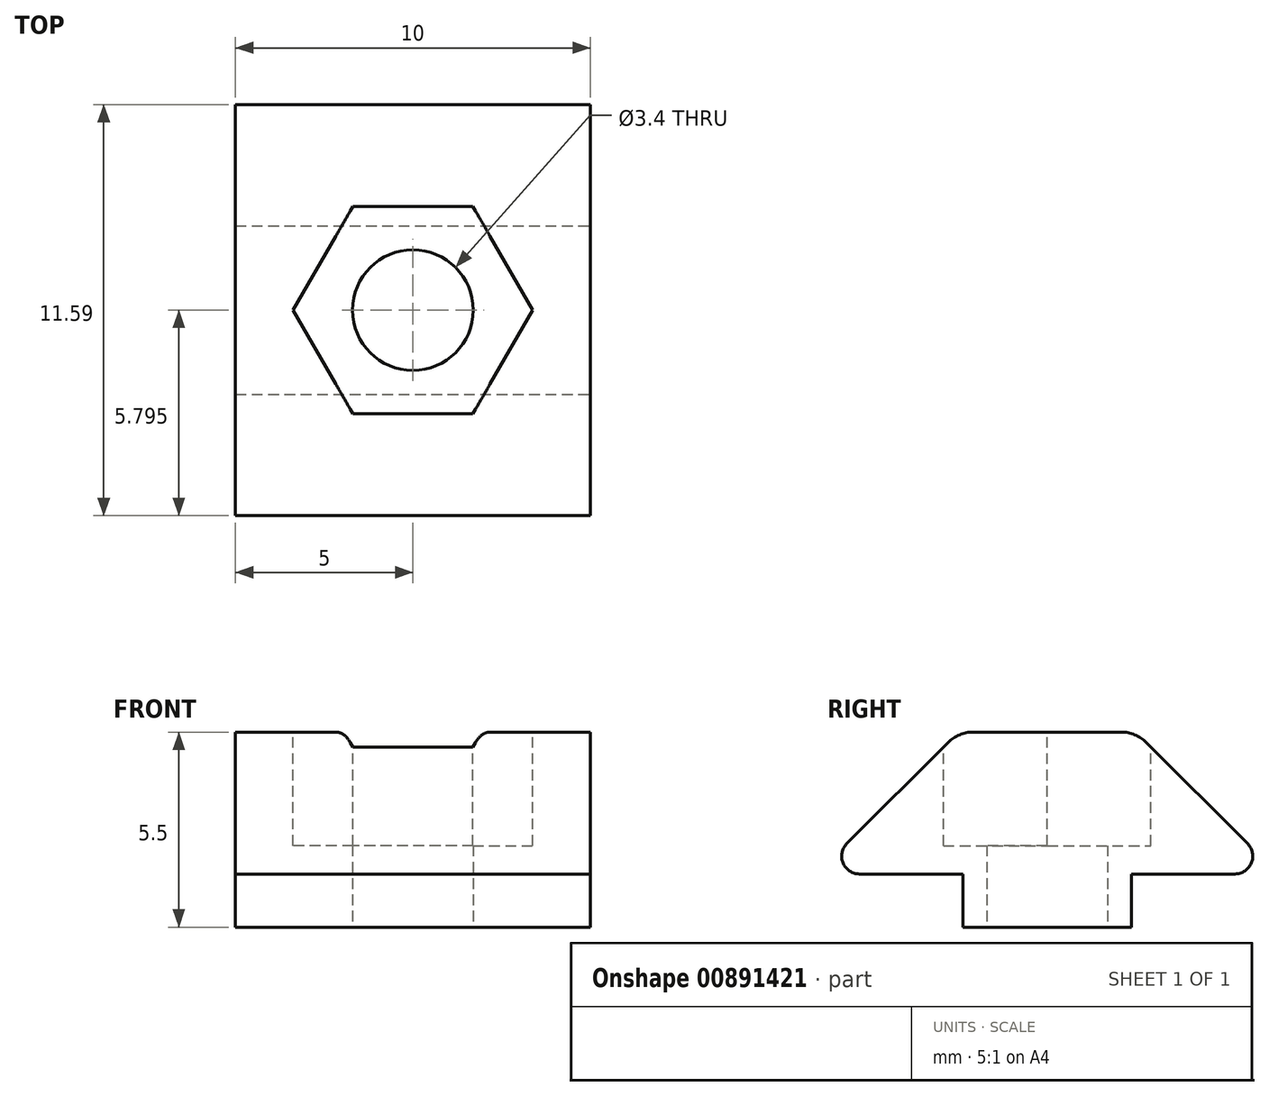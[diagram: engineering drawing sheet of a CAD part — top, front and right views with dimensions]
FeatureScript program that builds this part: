
annotation { "Feature Type Name" : "Feature", "Feature Type Description" : "" }
export const myFeature = defineFeature(function(context is Context, id is Id, definition is map)
    precondition{}
    {
        {
            var Q0;
            Q0=qCreatedBy(makeId("Top.planeOp"),FACE);
            var sketch = newSketch(context, id + "F0", { "sketchPlane" : qUnion([Q0])});
            skLineSegment(sketch, "E0.bottom", {"start": v(0, 4.75) * mm, "end": v(10, 4.75) * mm});
            skLineSegment(sketch, "E0.top", {"start": v(0, 0) * mm, "end": v(10, 0) * mm});
            skLineSegment(sketch, "E0.left", {"start": v(0, 4.75) * mm, "end": v(0, 0) * mm});
            skLineSegment(sketch, "E0.right", {"start": v(10, 4.75) * mm, "end": v(10, 0) * mm});
            skSolve(sketch);
        }
        {
            var Q0;
            Q0=makeQuery(id+"F0.imprint","IMPRINT",FACE,{"disambiguationData":[TD([[makeQuery(id+"F0.imprint","IMPRINT",EDGE,{"derivedFrom":sQuery(id+"F0.wireOp",EDGE,"E0.bottom")}),-1.0]])]});
            extrude(context, id + "F1", {"entities" : qUnion([Q0]), "depth" : 1.5 * mm, "offsetDistance" : 25 * mm});
        }
        {
            var Q0;
            Q0=makeQuery(id+"F1.opExtrude","CAP_FACE",FACE,{"disambiguationData":[OSD([sQuery(id+"F0.wireOp",EDGE,"E0.bottom"),sQuery(id+"F0.wireOp",EDGE,"E0.top"),sQuery(id+"F0.wireOp",EDGE,"E0.left"),sQuery(id+"F0.wireOp",EDGE,"E0.right")])],"isStart":false});
            var sketch = newSketch(context, id + "F2", { "sketchPlane" : qUnion([Q0])});
            skLineSegment(sketch, "E1.bottom", {"start": v(0, 8.88) * mm, "end": v(10, 8.88) * mm});
            skLineSegment(sketch, "E1.top", {"start": v(0, -4.13) * mm, "end": v(10, -4.13) * mm});
            skLineSegment(sketch, "E1.left", {"start": v(0, 8.87) * mm, "end": v(0, -4.13) * mm});
            skLineSegment(sketch, "E1.right", {"start": v(10, 8.88) * mm, "end": v(10, -4.13) * mm});
            skPoint(sketch, "E2", {"position": v(10, 2.37) * mm});
            skPoint(sketch, "E3", {"position": v(0, 2.37) * mm});
            skLineSegment(sketch, "E4", {"start": v(0, 2.37) * mm, "end": v(10, 2.37) * mm, "construction": true});
            skSolve(sketch);
        }
        {
            var Q0;
            {var subQ0=sQuery(id+"F2.wireOp",EDGE,"E1.top");Q0=makeQuery(id+"F2.imprint","IMPRINT",FACE,{"disambiguationData":[TD([[makeQuery(id+"F2.imprint","IMPRINT",EDGE,{"derivedFrom":subQ0}),1.0]])]});}
            var Q1;
            {var subQ1=makeQuery(id+"F1.opExtrude","CAP_EDGE",EDGE,{"disambiguationData":[OSD([sQuery(id+"F0.wireOp",EDGE,"E0.bottom")])],"isStart":false});Q1=makeQuery(id+"F2.imprint","IMPRINT",FACE,{"disambiguationData":[TD([[makeQuery(id+"F2.imprint","IMPRINT",EDGE,{"derivedFrom":subQ1}),-1.0]])]});}
            var Q2;
            {var subQ0=sQuery(id+"F2.wireOp",EDGE,"E1.bottom");Q2=makeQuery(id+"F2.imprint","IMPRINT",FACE,{"disambiguationData":[TD([[makeQuery(id+"F2.imprint","IMPRINT",EDGE,{"derivedFrom":subQ0}),-1.0]])]});}
            extrude(context, id + "F3", {"entities" : qUnion([Q0, Q1, Q2]), "operationType" : NewBodyOperationType.ADD, "depth" : 4 * mm, "offsetDistance" : 25 * mm});
        }
        {
            var Q0;
            Q0=makeQuery(id+"F3.opExtrude","CAP_EDGE",EDGE,{"disambiguationData":[OSD([sQuery(id+"F2.wireOp",EDGE,"E1.bottom")])],"isStart":false});
            var Q1;
            Q1=makeQuery(id+"F3.opExtrude","CAP_EDGE",EDGE,{"disambiguationData":[OSD([sQuery(id+"F2.wireOp",EDGE,"E1.top")])],"isStart":false});
            chamfer(context, id + "F4", {"entities" : qUnion([Q0, Q1]), "width" : 4 * mm, "tangentPropagation" : true});
        }
        {
            var Q0;
            Q0=makeQuery(id+"F3.opExtrude","CAP_FACE",FACE,{"disambiguationData":[OSD([sQuery(id+"F2.wireOp",EDGE,"E1.bottom"),sQuery(id+"F2.wireOp",EDGE,"E1.top"),sQuery(id+"F2.wireOp",EDGE,"E1.left"),sQuery(id+"F2.wireOp",EDGE,"E1.right")])],"isStart":false});
            var sketch = newSketch(context, id + "F5", { "sketchPlane" : qUnion([Q0])});
            skLineSegment(sketch, "E5", {"start": v(5, 4.88) * mm, "end": v(5, -0.13) * mm, "construction": true});
            skLineSegment(sketch, "E6", {"start": v(0, 2.38) * mm, "end": v(10, 2.38) * mm, "construction": true});
            skCircle(sketch, "E7.cCircle", {"center": v(5, 2.38) * mm, "radius": 2.93 * mm, "construction": true});
            skLineSegment(sketch, "E7.0", {"start": v(3.31, 5.3) * mm, "end": v(6.69, 5.3) * mm});
            skLineSegment(sketch, "E7.1", {"start": v(6.69, 5.3) * mm, "end": v(8.38, 2.38) * mm});
            skLineSegment(sketch, "E7.2", {"start": v(8.38, 2.38) * mm, "end": v(6.69, -0.55) * mm});
            skLineSegment(sketch, "E7.3", {"start": v(6.69, -0.55) * mm, "end": v(3.31, -0.55) * mm});
            skLineSegment(sketch, "E7.4", {"start": v(3.31, -0.55) * mm, "end": v(1.62, 2.38) * mm});
            skLineSegment(sketch, "E7.5", {"start": v(1.62, 2.38) * mm, "end": v(3.31, 5.3) * mm});
            skPoint(sketch, "E7.0.midPoint", {"position": v(5, 5.3) * mm});
            skSolve(sketch);
        }
        {
            var Q0;
            {var subQ0=sQuery(id+"F5.wireOp",EDGE,"E7.0");Q0=makeQuery(id+"F5.imprint","IMPRINT",FACE,{"disambiguationData":[TD([[makeQuery(id+"F5.imprint","IMPRINT",EDGE,{"derivedFrom":subQ0}),-1.0]])]});}
            var Q1;
            {var subQ8=sQuery(id+"F5.wireOp",EDGE,"E7.2");var subQ9=sQuery(id+"F5.wireOp",EDGE,"E7.1");var subQ10=makeQuery(id+"F5.imprint","INTERSECT",VERTEX,{"derivedFrom":[subQ9,subQ8]});Q1=makeQuery(id+"F5.imprint","IMPRINT",FACE,{"disambiguationData":[TD([[makeQuery(id+"F5.imprint","IMPRINT",EDGE,{"disambiguationData":[TD([[subQ10,1.0]])],"derivedFrom":subQ9}),-1.0]])]});}
            var Q2;
            {var subQ0=sQuery(id+"F5.wireOp",EDGE,"E7.3");Q2=makeQuery(id+"F5.imprint","IMPRINT",FACE,{"disambiguationData":[TD([[makeQuery(id+"F5.imprint","IMPRINT",EDGE,{"derivedFrom":subQ0}),-1.0]])]});}
            var Q3;
            {var subQ0=sQuery(id+"F2.wireOp",EDGE,"E1.top");var subQ1=sQuery(id+"F2.wireOp",EDGE,"E1.left");var subQ2=sQuery(id+"F2.wireOp",EDGE,"E1.right");Q3=makeQuery(id+"F3.boolean.opBoolean","SPLIT",FACE,{"disambiguationData":[TD([makeQuery(id+"F1.opExtrude","SWEPT_FACE",FACE,{"disambiguationData":[OSD([sQuery(id+"F0.wireOp",EDGE,"E0.top")])]})])],"derivedFrom":makeQuery(id+"F3.opExtrude","CAP_FACE",FACE,{"disambiguationData":[OSD([sQuery(id+"F2.wireOp",EDGE,"E1.bottom"),subQ0,subQ1,subQ2])],"isStart":true})});}
            extrude(context, id + "F6", {"entities" : qUnion([Q0, Q1, Q2]), "operationType" : NewBodyOperationType.REMOVE, "endBound" : BoundingType.UP_TO_SURFACE, "oppositeDirection" : true, "depth" : 3.1 * mm, "endBoundEntityFace" : qUnion([Q3]), "hasOffset" : true, "offsetDistance" : 0.8 * mm});
        }
        {
            var Q0;
            Q0=makeQuery(id+"F1.opExtrude","CAP_FACE",FACE,{"disambiguationData":[OSD([sQuery(id+"F0.wireOp",EDGE,"E0.bottom"),sQuery(id+"F0.wireOp",EDGE,"E0.top"),sQuery(id+"F0.wireOp",EDGE,"E0.left"),sQuery(id+"F0.wireOp",EDGE,"E0.right")])],"isStart":true});
            var sketch = newSketch(context, id + "F7", { "sketchPlane" : qUnion([Q0])});
            skLineSegment(sketch, "E8", {"start": v(5, 0) * mm, "end": v(5, -4.75) * mm, "construction": true});
            skCircle(sketch, "E9", {"center": v(5, -2.38) * mm, "radius": 1.7 * mm});
            skSolve(sketch);
        }
        {
            var Q0;
            Q0=makeQuery(id+"F7.imprint","IMPRINT",FACE,{"disambiguationData":[TD([[makeQuery(id+"F7.imprint","IMPRINT",EDGE,{"derivedFrom":sQuery(id+"F7.wireOp",EDGE,"E9")}),1.0]])]});
            extrude(context, id + "F8", {"entities" : qUnion([Q0]), "operationType" : NewBodyOperationType.REMOVE, "endBound" : BoundingType.THROUGH_ALL, "oppositeDirection" : true, "depth" : 25 * mm, "offsetDistance" : 25 * mm});
        }
        {
            var Q0;
            {var subQ0=sQuery(id+"F2.wireOp",EDGE,"E1.bottom");var subQ1=sQuery(id+"F2.wireOp",EDGE,"E1.left");var subQ2=sQuery(id+"F2.wireOp",EDGE,"E1.right");Q0=makeQuery(id+"F4.opChamfer","BLEND_EDGE",EDGE,{"blendedFrom":[makeQuery(id+"F3.opExtrude","CAP_EDGE",EDGE,{"disambiguationData":[OSD([subQ0])],"isStart":false}),makeQuery(id+"F3.boolean.opBoolean","SPLIT",FACE,{"disambiguationData":[TD([makeQuery(id+"F1.opExtrude","SWEPT_FACE",FACE,{"disambiguationData":[OSD([sQuery(id+"F0.wireOp",EDGE,"E0.bottom")])]})])],"derivedFrom":makeQuery(id+"F3.opExtrude","CAP_FACE",FACE,{"disambiguationData":[OSD([subQ0,sQuery(id+"F2.wireOp",EDGE,"E1.top"),subQ1,subQ2])],"isStart":true})})],"blendedInto":[makeQuery(id+"F3.boolean.opBoolean","SPLIT",FACE,{"disambiguationData":[TD([makeQuery(id+"F1.opExtrude","SWEPT_FACE",FACE,{"disambiguationData":[OSD([sQuery(id+"F0.wireOp",EDGE,"E0.bottom")])]})])],"derivedFrom":makeQuery(id+"F3.opExtrude","CAP_FACE",FACE,{"disambiguationData":[OSD([subQ0,sQuery(id+"F2.wireOp",EDGE,"E1.top"),subQ1,subQ2])],"isStart":true})})]});}
            var Q1;
            {var subQ0=sQuery(id+"F2.wireOp",EDGE,"E1.top");var subQ1=sQuery(id+"F2.wireOp",EDGE,"E1.left");var subQ2=sQuery(id+"F2.wireOp",EDGE,"E1.right");Q1=makeQuery(id+"F4.opChamfer","BLEND_EDGE",EDGE,{"blendedFrom":[makeQuery(id+"F3.opExtrude","CAP_EDGE",EDGE,{"disambiguationData":[OSD([subQ0])],"isStart":false}),makeQuery(id+"F3.boolean.opBoolean","SPLIT",FACE,{"disambiguationData":[TD([makeQuery(id+"F1.opExtrude","SWEPT_FACE",FACE,{"disambiguationData":[OSD([sQuery(id+"F0.wireOp",EDGE,"E0.top")])]})])],"derivedFrom":makeQuery(id+"F3.opExtrude","CAP_FACE",FACE,{"disambiguationData":[OSD([sQuery(id+"F2.wireOp",EDGE,"E1.bottom"),subQ0,subQ1,subQ2])],"isStart":true})})],"blendedInto":[makeQuery(id+"F3.boolean.opBoolean","SPLIT",FACE,{"disambiguationData":[TD([makeQuery(id+"F1.opExtrude","SWEPT_FACE",FACE,{"disambiguationData":[OSD([sQuery(id+"F0.wireOp",EDGE,"E0.top")])]})])],"derivedFrom":makeQuery(id+"F3.opExtrude","CAP_FACE",FACE,{"disambiguationData":[OSD([sQuery(id+"F2.wireOp",EDGE,"E1.bottom"),subQ0,subQ1,subQ2])],"isStart":true})})]});}
            fillet(context, id + "F9", {"entities" : qUnion([Q0, Q1]), "radius" : 0.5 * mm, "tangentPropagation" : true, "allowEdgeOverflow" : false});
        }
        {
            var Q0;
            {var subQ0=sQuery(id+"F2.wireOp",EDGE,"E1.left");var subQ1=sQuery(id+"F2.wireOp",EDGE,"E1.bottom");var subQ2=makeQuery(id+"F3.opExtrude","CAP_FACE",FACE,{"disambiguationData":[OSD([subQ1,sQuery(id+"F2.wireOp",EDGE,"E1.top"),subQ0,sQuery(id+"F2.wireOp",EDGE,"E1.right")])],"isStart":false});Q0=makeQuery(id+"F6.boolean.opBoolean","SPLIT",EDGE,{"disambiguationData":[TD([makeQuery(id+"F1.opExtrude","SWEPT_FACE",FACE,{"disambiguationData":[OSD([sQuery(id+"F0.wireOp",EDGE,"E0.left")])]})])],"derivedFrom":makeQuery(id+"F4.opChamfer","BLEND_EDGE",EDGE,{"blendedFrom":[makeQuery(id+"F3.opExtrude","CAP_EDGE",EDGE,{"disambiguationData":[OSD([subQ1])],"isStart":false}),subQ2],"blendedInto":[subQ2]})});}
            var Q1;
            {var subQ0=sQuery(id+"F2.wireOp",EDGE,"E1.top");var subQ1=sQuery(id+"F2.wireOp",EDGE,"E1.left");var subQ2=makeQuery(id+"F3.opExtrude","CAP_FACE",FACE,{"disambiguationData":[OSD([sQuery(id+"F2.wireOp",EDGE,"E1.bottom"),subQ0,subQ1,sQuery(id+"F2.wireOp",EDGE,"E1.right")])],"isStart":false});Q1=makeQuery(id+"F6.boolean.opBoolean","SPLIT",EDGE,{"disambiguationData":[TD([makeQuery(id+"F1.opExtrude","SWEPT_FACE",FACE,{"disambiguationData":[OSD([sQuery(id+"F0.wireOp",EDGE,"E0.left")])]})])],"derivedFrom":makeQuery(id+"F4.opChamfer","BLEND_EDGE",EDGE,{"blendedFrom":[makeQuery(id+"F3.opExtrude","CAP_EDGE",EDGE,{"disambiguationData":[OSD([subQ0])],"isStart":false}),subQ2],"blendedInto":[subQ2]})});}
            var Q2;
            {var subQ0=sQuery(id+"F2.wireOp",EDGE,"E1.top");var subQ1=sQuery(id+"F2.wireOp",EDGE,"E1.right");var subQ2=makeQuery(id+"F3.opExtrude","CAP_FACE",FACE,{"disambiguationData":[OSD([sQuery(id+"F2.wireOp",EDGE,"E1.bottom"),subQ0,sQuery(id+"F2.wireOp",EDGE,"E1.left"),subQ1])],"isStart":false});Q2=makeQuery(id+"F6.boolean.opBoolean","SPLIT",EDGE,{"disambiguationData":[TD([makeQuery(id+"F1.opExtrude","SWEPT_FACE",FACE,{"disambiguationData":[OSD([sQuery(id+"F0.wireOp",EDGE,"E0.right")])]})])],"derivedFrom":makeQuery(id+"F4.opChamfer","BLEND_EDGE",EDGE,{"blendedFrom":[makeQuery(id+"F3.opExtrude","CAP_EDGE",EDGE,{"disambiguationData":[OSD([subQ0])],"isStart":false}),subQ2],"blendedInto":[subQ2]})});}
            var Q3;
            {var subQ0=sQuery(id+"F2.wireOp",EDGE,"E1.right");var subQ1=sQuery(id+"F2.wireOp",EDGE,"E1.bottom");var subQ2=makeQuery(id+"F3.opExtrude","CAP_FACE",FACE,{"disambiguationData":[OSD([subQ1,sQuery(id+"F2.wireOp",EDGE,"E1.top"),sQuery(id+"F2.wireOp",EDGE,"E1.left"),subQ0])],"isStart":false});Q3=makeQuery(id+"F6.boolean.opBoolean","SPLIT",EDGE,{"disambiguationData":[TD([makeQuery(id+"F1.opExtrude","SWEPT_FACE",FACE,{"disambiguationData":[OSD([sQuery(id+"F0.wireOp",EDGE,"E0.right")])]})])],"derivedFrom":makeQuery(id+"F4.opChamfer","BLEND_EDGE",EDGE,{"blendedFrom":[makeQuery(id+"F3.opExtrude","CAP_EDGE",EDGE,{"disambiguationData":[OSD([subQ1])],"isStart":false}),subQ2],"blendedInto":[subQ2]})});}
            fillet(context, id + "F10", {"entities" : qUnion([Q0, Q1, Q2, Q3]), "radius" : 1 * mm, "tangentPropagation" : true, "allowEdgeOverflow" : false});
        }
    });
